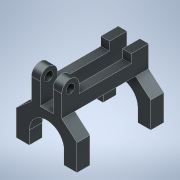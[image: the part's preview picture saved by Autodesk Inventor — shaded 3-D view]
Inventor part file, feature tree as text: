
AUTODESK INVENTOR PART (.ipt)
format: ipt  version: 2022.2 (Build 262287030, 287C)  size: 183,808 bytes
history: native  units: in
note: dims shown in document units (in); Inventor stores cm internally (conversion verified against a paired STEP export)
features: sketch x4, extrude x3, mirror x1, hole x1
ambient origin geometry x8: Origin, YZ Plane, XZ Plane, XY Plane, X Axis, Y Axis, Z Axis, Center Point
bodies: Solid1 (feature_tree)
feature tree (9):
  extrude  "Extrusion1"  Depth=0.75in
  extrude  "Extrusion2"  Depth=1.25in
  extrude  "Extrusion3"  Depth=1.0in
  mirror  "Mirror1"
  hole  "Hole1"  [1 undecoded]
  sketch  "Sketch1"  dims[d0=3.5in d1=0.75in]
  sketch  "Sketch3"  dims[d2=1.5in d3=1.25in]
  sketch  "Sketch4"  dims[d4=0.75in d5=1.0in]
  sketch  "Sketch5"  dims[d6=3.5in d7=0.75in d8=1.75in d9=5.0in d10=0.0in d12=1.0in d13=1.0in d14=0.5in d15=0.75in d16=0.75in d17=0.0in d18=0.0in d19=1.0in d20=0.0in d21=0.5in d22=0.75in d23=0.375in d24=0.25in d25=0.5635in d26=1.0in d27=0.8108in]
note: 1 required parameter value undecoded (feature->parameter linkage not recoverable at this tier; creation-order binding heuristic only, values carry confidence <= 0.55)
